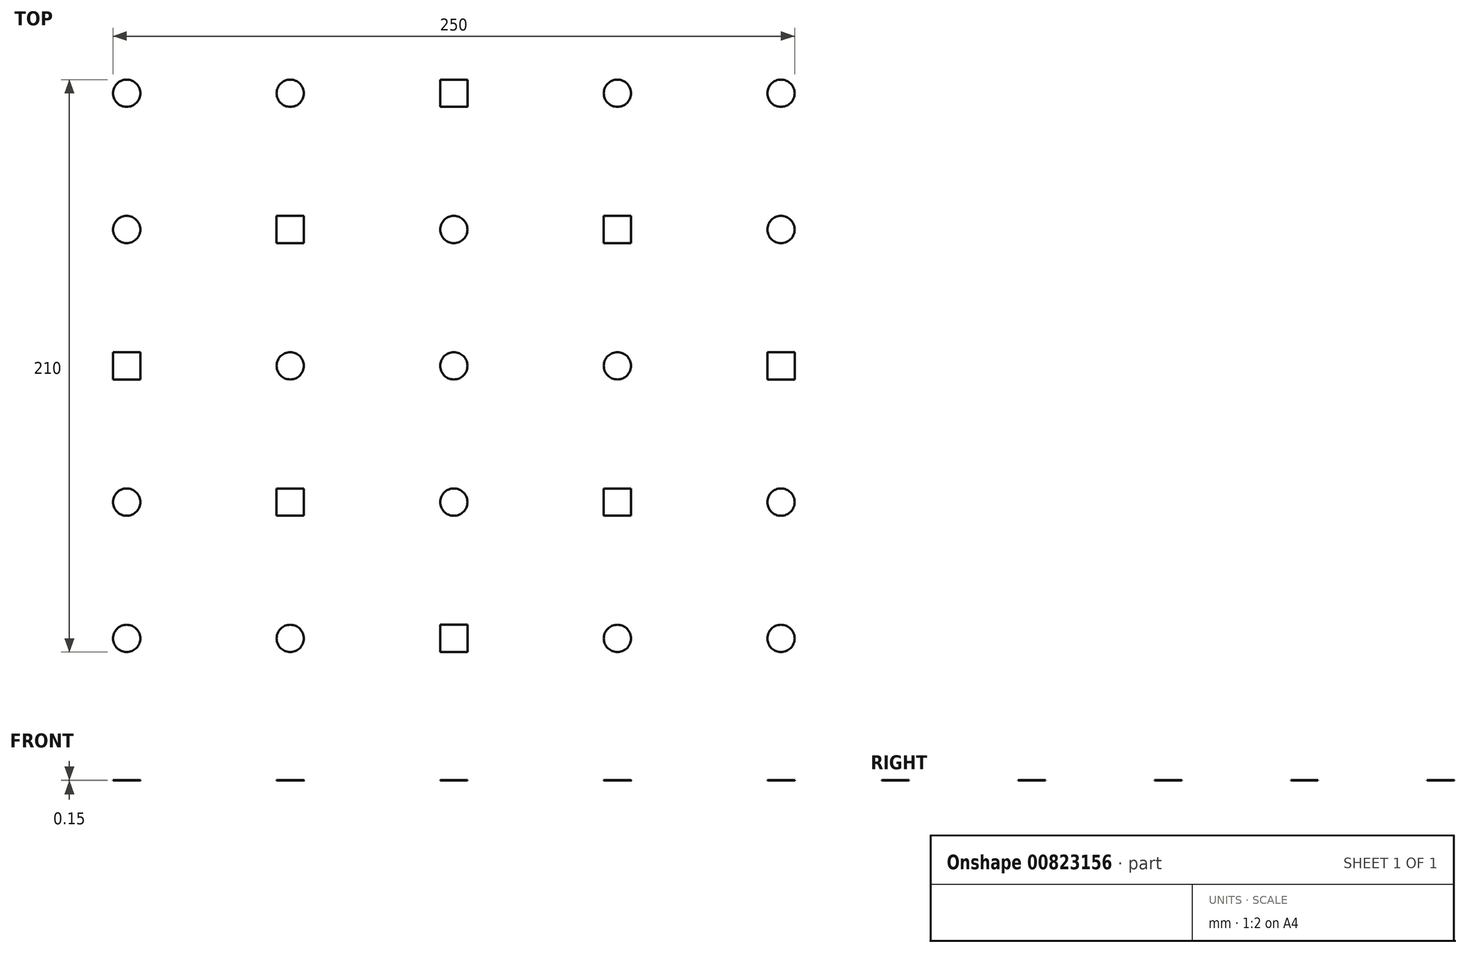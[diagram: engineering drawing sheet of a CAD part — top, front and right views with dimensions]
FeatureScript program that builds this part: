
annotation { "Feature Type Name" : "Feature", "Feature Type Description" : "" }
export const myFeature = defineFeature(function(context is Context, id is Id, definition is map)
    precondition{}
    {
        {
            var Q0;
            Q0=qCreatedBy(makeId("Top.planeOp"),FACE);
            var sketch = newSketch(context, id + "F0", { "sketchPlane" : qUnion([Q0])});
            skCircle(sketch, "E0", {"center": v(0, 0) * mm, "radius": 5 * mm});
            skLineSegment(sketch, "E1.bottom", {"start": v(-115, 5) * mm, "end": v(-125, 5) * mm});
            skLineSegment(sketch, "E1.top", {"start": v(-115, -5) * mm, "end": v(-125, -5) * mm});
            skLineSegment(sketch, "E1.left", {"start": v(-115, 5) * mm, "end": v(-115, -5) * mm});
            skLineSegment(sketch, "E1.right", {"start": v(-125, 5) * mm, "end": v(-125, -5) * mm});
            skPoint(sketch, "E1.middle", {"position": v(-120, 0) * mm});
            skLineSegment(sketch, "E2.MirrorCS", {"start": v(115, -5) * mm, "end": v(125, -5) * mm});
            skLineSegment(sketch, "E3.MirrorCS", {"start": v(115, 5) * mm, "end": v(115, -5) * mm});
            skLineSegment(sketch, "E4.MirrorCS", {"start": v(125, 5) * mm, "end": v(125, -5) * mm});
            skLineSegment(sketch, "E5.MirrorCS", {"start": v(115, 5) * mm, "end": v(125, 5) * mm});
            skPoint(sketch, "E6.MirrorP", {"position": v(120, 0) * mm});
            skLineSegment(sketch, "E7.bottom", {"start": v(5, 95) * mm, "end": v(-5, 95) * mm});
            skLineSegment(sketch, "E7.top", {"start": v(5, 105) * mm, "end": v(-5, 105) * mm});
            skLineSegment(sketch, "E7.left", {"start": v(5, 95) * mm, "end": v(5, 105) * mm});
            skLineSegment(sketch, "E7.right", {"start": v(-5, 95) * mm, "end": v(-5, 105) * mm});
            skPoint(sketch, "E7.middle", {"position": v(0, 100) * mm});
            skLineSegment(sketch, "E8.MirrorCS", {"start": v(5, -95) * mm, "end": v(-5, -95) * mm});
            skLineSegment(sketch, "E9.MirrorCS", {"start": v(5, -105) * mm, "end": v(-5, -105) * mm});
            skLineSegment(sketch, "E10.MirrorCS", {"start": v(-5, -95) * mm, "end": v(-5, -105) * mm});
            skLineSegment(sketch, "E11.MirrorCS", {"start": v(5, -95) * mm, "end": v(5, -105) * mm});
            skPoint(sketch, "E12.MirrorP", {"position": v(0, -100) * mm});
            skCircle(sketch, "E13", {"center": v(-120, 100) * mm, "radius": 5 * mm});
            skCircle(sketch, "E14.MirrorC", {"center": v(120, 100) * mm, "radius": 5 * mm});
            skCircle(sketch, "E15.MirrorC", {"center": v(-120, -100) * mm, "radius": 5 * mm});
            skCircle(sketch, "E16.MirrorC", {"center": v(120, -100) * mm, "radius": 5 * mm});
            skLineSegment(sketch, "E17", {"start": v(-120, 100) * mm, "end": v(0, 0) * mm, "construction": true});
            skLineSegment(sketch, "E18.bottom", {"start": v(-65, 45) * mm, "end": v(-55, 45) * mm});
            skLineSegment(sketch, "E18.top", {"start": v(-65, 55) * mm, "end": v(-55, 55) * mm});
            skLineSegment(sketch, "E18.left", {"start": v(-65, 45) * mm, "end": v(-65, 55) * mm});
            skLineSegment(sketch, "E18.right", {"start": v(-55, 45) * mm, "end": v(-55, 55) * mm});
            skPoint(sketch, "E18.middle", {"position": v(-60, 50) * mm});
            skCircle(sketch, "E19", {"center": v(-120, 50) * mm, "radius": 5 * mm});
            skCircle(sketch, "E20", {"center": v(-60, 100) * mm, "radius": 5 * mm});
            skCircle(sketch, "E21", {"center": v(-60, 0) * mm, "radius": 5 * mm});
            skCircle(sketch, "E22.MirrorC", {"center": v(60, 100) * mm, "radius": 5 * mm});
            skCircle(sketch, "E23.MirrorC", {"center": v(120, 50) * mm, "radius": 5 * mm});
            skCircle(sketch, "E24.MirrorC", {"center": v(-120, -50) * mm, "radius": 5 * mm});
            skCircle(sketch, "E25.MirrorC", {"center": v(-60, -100) * mm, "radius": 5 * mm});
            skCircle(sketch, "E26.MirrorC", {"center": v(60, -100) * mm, "radius": 5 * mm});
            skCircle(sketch, "E27.MirrorC", {"center": v(120, -50) * mm, "radius": 5 * mm});
            skLineSegment(sketch, "E28.MirrorCS", {"start": v(65, 45) * mm, "end": v(65, 55) * mm});
            skLineSegment(sketch, "E29.MirrorCS", {"start": v(65, 55) * mm, "end": v(55, 55) * mm});
            skLineSegment(sketch, "E30.MirrorCS", {"start": v(65, 45) * mm, "end": v(55, 45) * mm});
            skLineSegment(sketch, "E31.MirrorCS", {"start": v(55, 45) * mm, "end": v(55, 55) * mm});
            skPoint(sketch, "E32.MirrorP", {"position": v(-60, -50) * mm});
            skLineSegment(sketch, "E33.MirrorCS", {"start": v(-55, -45) * mm, "end": v(-55, -55) * mm});
            skLineSegment(sketch, "E34.MirrorCS", {"start": v(65, -45) * mm, "end": v(65, -55) * mm});
            skLineSegment(sketch, "E35.MirrorCS", {"start": v(65, -55) * mm, "end": v(55, -55) * mm});
            skLineSegment(sketch, "E36.MirrorCS", {"start": v(-65, -55) * mm, "end": v(-55, -55) * mm});
            skLineSegment(sketch, "E37.MirrorCS", {"start": v(-65, -45) * mm, "end": v(-65, -55) * mm});
            skLineSegment(sketch, "E38.MirrorCS", {"start": v(-65, -45) * mm, "end": v(-55, -45) * mm});
            skLineSegment(sketch, "E39.MirrorCS", {"start": v(65, -45) * mm, "end": v(55, -45) * mm});
            skLineSegment(sketch, "E40.MirrorCS", {"start": v(55, -45) * mm, "end": v(55, -55) * mm});
            skCircle(sketch, "E41", {"center": v(0, 50) * mm, "radius": 5 * mm});
            skCircle(sketch, "E42.MirrorC", {"center": v(0, -50) * mm, "radius": 5 * mm});
            skCircle(sketch, "E43.MirrorC", {"center": v(60, 0) * mm, "radius": 5 * mm});
            skSolve(sketch);
        }
        {
            var Q0;
            Q0 = qSketchRegion(id + "F0", true);
            extrude(context, id + "F1", {"entities" : qUnion([Q0]), "domain" : OperationDomain.MODEL, "flatOperationType" : FlatOperationType.REMOVE, "depth" : 0.15 * mm, "offsetDistance" : 25 * mm});
        }
    });
